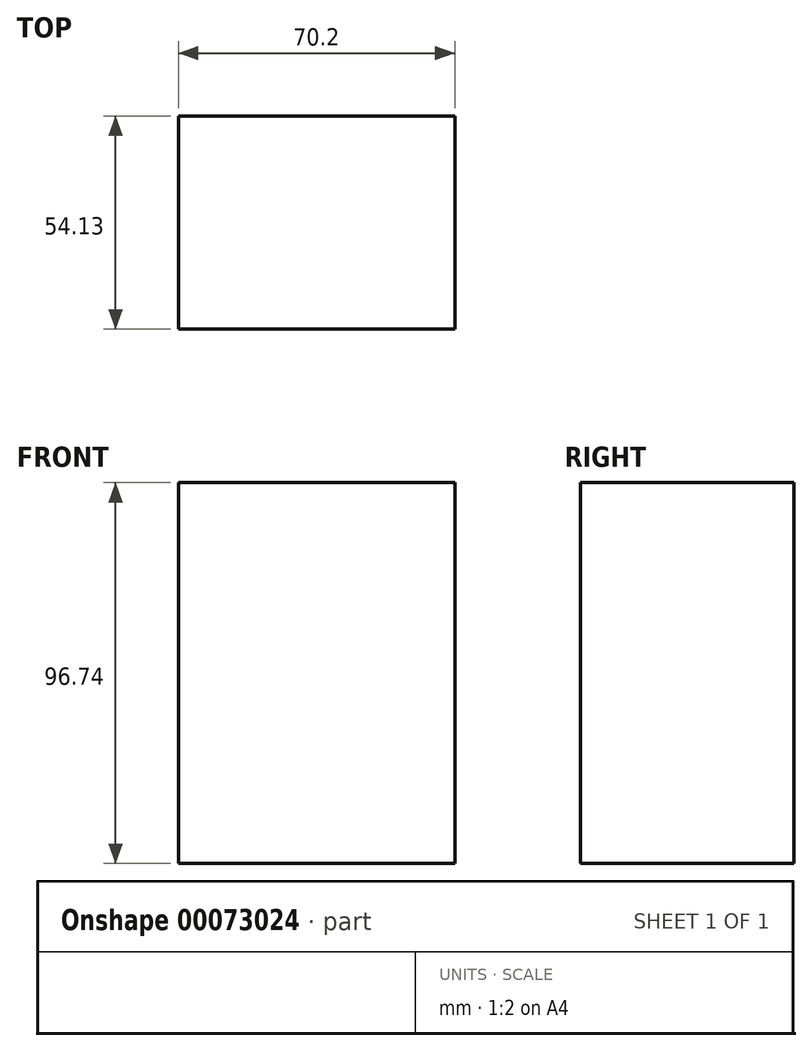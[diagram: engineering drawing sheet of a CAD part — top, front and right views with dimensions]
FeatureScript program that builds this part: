
annotation { "Feature Type Name" : "Feature", "Feature Type Description" : "" }
export const myFeature = defineFeature(function(context is Context, id is Id, definition is map)
    precondition{}
    {
        {
            var Q0;
            Q0=qCreatedBy(makeId("Right.planeOp"),FACE);
            var sketch = newSketch(context, id + "F0", { "sketchPlane" : qUnion([Q0])});
            skLineSegment(sketch, "E0.bottom", {"start": v(23.62, 45.29) * mm, "end": v(-30.51, 45.29) * mm});
            skLineSegment(sketch, "E0.top", {"start": v(23.62, -51.45) * mm, "end": v(-30.51, -51.45) * mm});
            skLineSegment(sketch, "E0.left", {"start": v(23.62, 45.29) * mm, "end": v(23.62, -51.45) * mm});
            skLineSegment(sketch, "E0.right", {"start": v(-30.51, 45.29) * mm, "end": v(-30.51, -51.45) * mm});
            skSolve(sketch);
        }
        {
            var Q0;
            Q0 = qSketchRegion(id + "F0", true);
            extrude(context, id + "F1", {"entities" : qUnion([Q0]), "depth" : 70.2 * mm});
        }
    });
